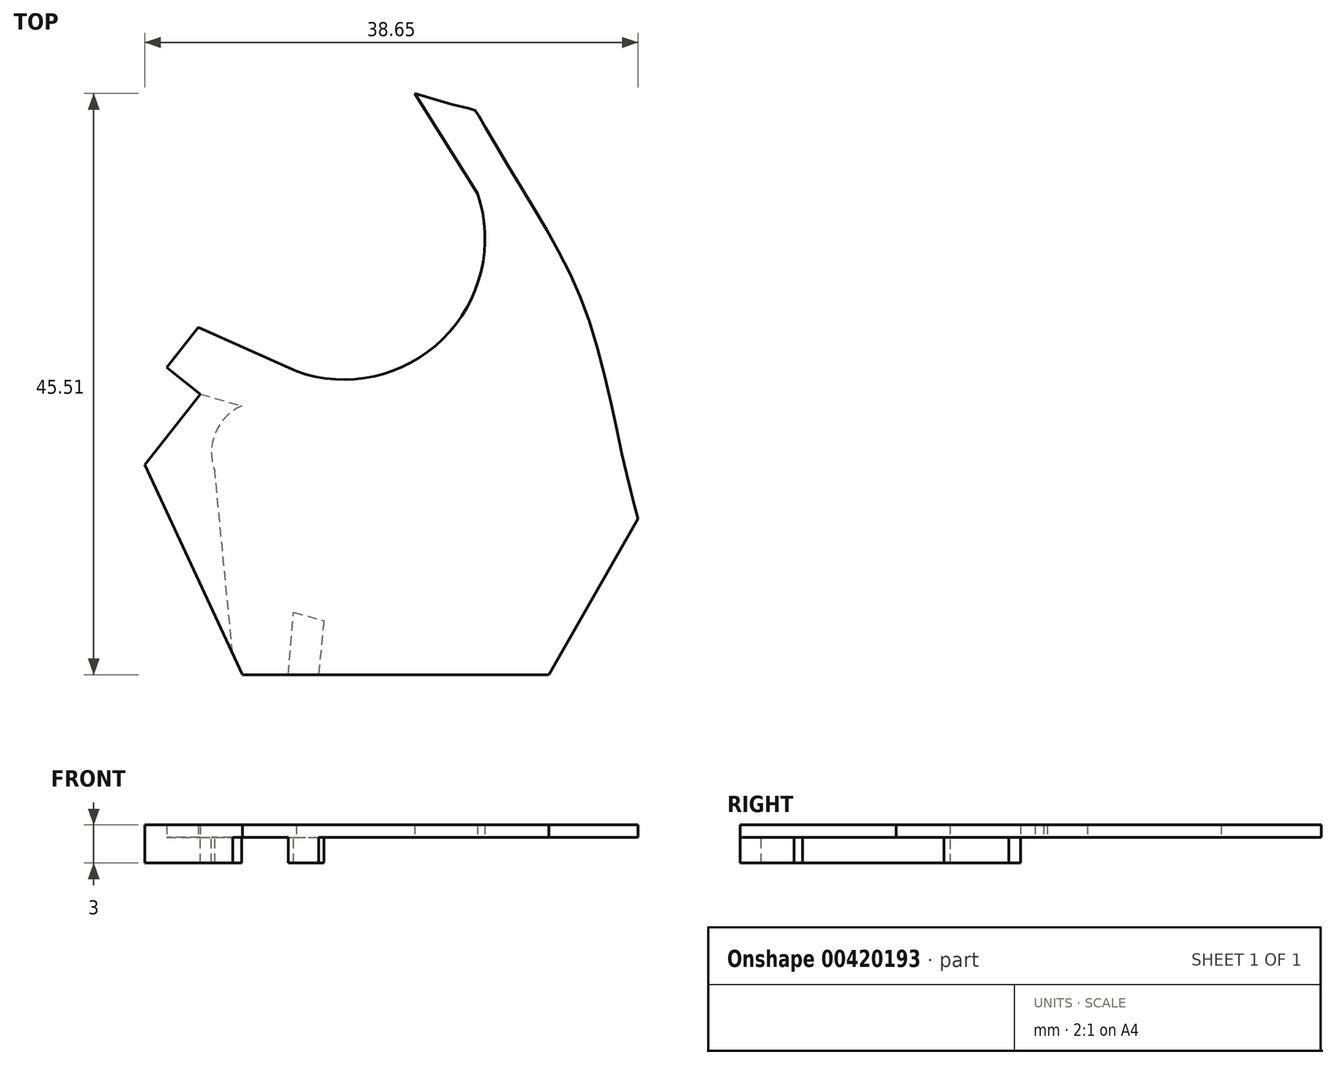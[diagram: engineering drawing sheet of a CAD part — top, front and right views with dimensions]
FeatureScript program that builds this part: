
annotation { "Feature Type Name" : "Feature", "Feature Type Description" : "" }
export const myFeature = defineFeature(function(context is Context, id is Id, definition is map)
    precondition{}
    {
        {
            var Q0;
            Q0=qCreatedBy(makeId("Top.planeOp"),FACE);
            var sketch = newSketch(context, id + "F0", { "sketchPlane" : qUnion([Q0])});
            skLineSegment(sketch, "E0", {"start": v(-18.43, -12.2) * mm, "end": v(5.57, -12.2) * mm});
            skLineSegment(sketch, "E1", {"start": v(5.57, -12.2) * mm, "end": v(12.57, 0) * mm});
            skLineSegment(sketch, "E2", {"start": v(-18.43, -12.2) * mm, "end": v(-26.08, 4.22) * mm});
            skLineSegment(sketch, "E3", {"start": v(-26.08, 4.22) * mm, "end": v(-21.72, 9.75) * mm});
            skLineSegment(sketch, "E4", {"start": v(-21.72, 9.75) * mm, "end": v(-24.38, 11.84) * mm});
            skLineSegment(sketch, "E5", {"start": v(-24.38, 11.84) * mm, "end": v(-21.9, 14.99) * mm});
            skFitSpline(sketch, "E6", {"points": [v(-4.93, 33.3) * mm, v(0, 31.68) * mm, v(3.69, 25.48) * mm, v(8.53, 16.07) * mm, v(11.5, 4.22) * mm, v(12.57, 0) * mm], "startDerivative": vector(89.38, -29.29) * mm, "endDerivative": vector(6.63, -23.97) * mm});
            skLineSegment(sketch, "E7", {"start": v(-21.9, 14.99) * mm, "end": v(-14.21, 11.55) * mm});
            skLineSegment(sketch, "E8", {"start": v(0, 25.48) * mm, "end": v(-4.93, 33.3) * mm});
            skPoint(sketch, "E9", {"position": v(-14.21, 11.55) * mm});
            skPoint(sketch, "E10", {"position": v(0, 25.48) * mm});
            skPoint(sketch, "E11", {"position": v(-2.8, 14.02) * mm});
            skArc(sketch, "E12", {"start": v(-14.21, 11.55) * mm, "mid": v(-2.74, 14.06) * mm, "end": v(0, 25.48) * mm});
            skLineSegment(sketch, "E13", {"start": v(-14.85, -12.2) * mm, "end": v(-13.57, 2.92) * mm});
            skCircle(sketch, "E14", {"center": v(-16.86, 5.18) * mm, "radius": 4 * mm});
            skLineSegment(sketch, "E15", {"start": v(-19.2, -10.55) * mm, "end": v(-20.6, 3.74) * mm});
            skLineSegment(sketch, "E16", {"start": v(-10.17, 10.9) * mm, "end": v(-12.47, -12.2) * mm});
            skLineSegment(sketch, "E17", {"start": v(-21.72, 9.75) * mm, "end": v(-10.6, 6.63) * mm});
            skLineSegment(sketch, "E18", {"start": v(-14.43, -7.32) * mm, "end": v(-12.05, -7.99) * mm});
            skSolve(sketch);
        }
        {
            var Q0;
            {var subQ1=sQuery(id+"F0.wireOp",EDGE,"E1");Q0=makeQuery(id+"F0.imprint","IMPRINT",FACE,{"disambiguationData":[TD([[makeQuery(id+"F0.imprint","IMPRINT",EDGE,{"derivedFrom":subQ1}),1.0]])]});}
            var Q1;
            {var subQ0=sQuery(id+"F0.wireOp",EDGE,"E13");Q1=makeQuery(id+"F0.imprint","IMPRINT",FACE,{"disambiguationData":[TD([[makeQuery(id+"F0.imprint","IMPRINT",EDGE,{"derivedFrom":subQ0}),1.0]])]});}
            var Q2;
            {var subQ0=sQuery(id+"F0.wireOp",EDGE,"E14");var subQ1=makeQuery(id+"F0.imprint","INTERSECT",VERTEX,{"derivedFrom":[sQuery(id+"F0.wireOp",EDGE,"E13"),subQ0]});Q2=makeQuery(id+"F0.imprint","IMPRINT",FACE,{"disambiguationData":[TD([[makeQuery(id+"F0.imprint","IMPRINT",EDGE,{"disambiguationData":[TD([[subQ1,1.0]])],"derivedFrom":subQ0}),1.0]])]});}
            var Q3;
            {var subQ6=sQuery(id+"F0.wireOp",EDGE,"E3");Q3=makeQuery(id+"F0.imprint","IMPRINT",FACE,{"disambiguationData":[TD([[makeQuery(id+"F0.imprint","IMPRINT",EDGE,{"derivedFrom":subQ6}),-1.0]])]});}
            var Q4;
            {var subQ4=sQuery(id+"F0.wireOp",EDGE,"E4");Q4=makeQuery(id+"F0.imprint","IMPRINT",FACE,{"disambiguationData":[TD([[makeQuery(id+"F0.imprint","IMPRINT",EDGE,{"derivedFrom":subQ4}),-1.0]])]});}
            var Q5;
            {var subQ0=sQuery(id+"F0.wireOp",EDGE,"E17");var subQ1=sQuery(id+"F0.wireOp",EDGE,"E14");var subQ2=makeQuery(id+"F0.imprint","INTERSECT",VERTEX,{"disambiguationData":[OD(0.0)],"derivedFrom":[subQ1,subQ0]});Q5=makeQuery(id+"F0.imprint","IMPRINT",FACE,{"disambiguationData":[TD([[makeQuery(id+"F0.imprint","IMPRINT",EDGE,{"disambiguationData":[TD([[subQ2,1.0]])],"derivedFrom":subQ1}),1.0]])]});}
            var Q6;
            {var subQ1=sQuery(id+"F0.wireOp",EDGE,"E13");Q6=makeQuery(id+"F0.imprint","IMPRINT",FACE,{"disambiguationData":[TD([[makeQuery(id+"F0.imprint","IMPRINT",EDGE,{"derivedFrom":subQ1}),-1.0]])]});}
            var Q7;
            {var subQ7=sQuery(id+"F0.wireOp",EDGE,"E18");Q7=makeQuery(id+"F0.imprint","IMPRINT",FACE,{"disambiguationData":[TD([[makeQuery(id+"F0.imprint","IMPRINT",EDGE,{"derivedFrom":subQ7}),1.0]])]});}
            extrude(context, id + "F1", {"entities" : qUnion([Q0, Q1, Q2, Q3, Q4, Q5, Q6, Q7]), "depth" : 1 * mm});
        }
        {
            var Q0;
            {var subQ6=sQuery(id+"F0.wireOp",EDGE,"E3");Q0=makeQuery(id+"F0.imprint","IMPRINT",FACE,{"disambiguationData":[TD([[makeQuery(id+"F0.imprint","IMPRINT",EDGE,{"derivedFrom":subQ6}),-1.0]])]});}
            var Q1;
            {var subQ1=sQuery(id+"F0.wireOp",EDGE,"E13");Q1=makeQuery(id+"F0.imprint","IMPRINT",FACE,{"disambiguationData":[TD([[makeQuery(id+"F0.imprint","IMPRINT",EDGE,{"derivedFrom":subQ1}),-1.0]])]});}
            extrude(context, id + "F2", {"entities" : qUnion([Q0, Q1]), "operationType" : NewBodyOperationType.ADD, "depth" : 0 * mm, "hasSecondDirection" : true, "secondDirectionOppositeDirection" : true, "secondDirectionDepth" : 2 * mm});
        }
    });
